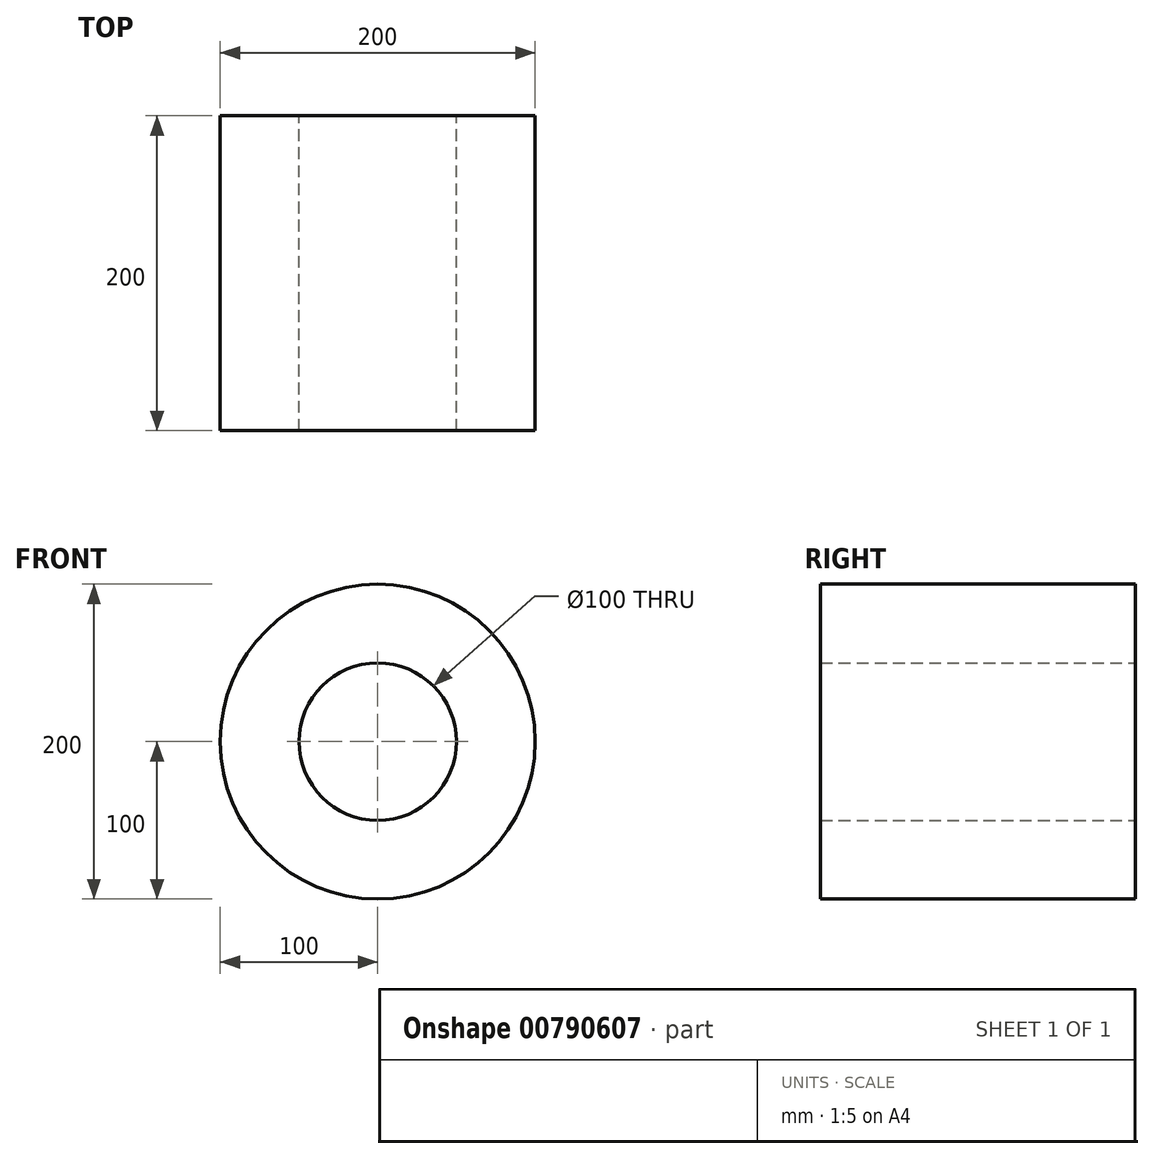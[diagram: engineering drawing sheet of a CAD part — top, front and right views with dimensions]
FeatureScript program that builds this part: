
annotation { "Feature Type Name" : "Feature", "Feature Type Description" : "" }
export const myFeature = defineFeature(function(context is Context, id is Id, definition is map)
    precondition{}
    {
        {
            var Q0;
            Q0=qCreatedBy(makeId("Front.planeOp"),FACE);
            var sketch = newSketch(context, id + "F0", { "sketchPlane" : qUnion([Q0])});
            skCircle(sketch, "E0", {"center": v(0, 0) * mm, "radius": 100 * mm});
            skCircle(sketch, "E1", {"center": v(0, 0) * mm, "radius": 50 * mm});
            skSolve(sketch);
        }
        {
            var Q0;
            Q0 = qSketchRegion(id + "F0", true);
            extrude(context, id + "F1", {"entities" : qUnion([Q0]), "depth" : 200 * mm, "offsetDistance" : 25 * mm});
        }
    });
